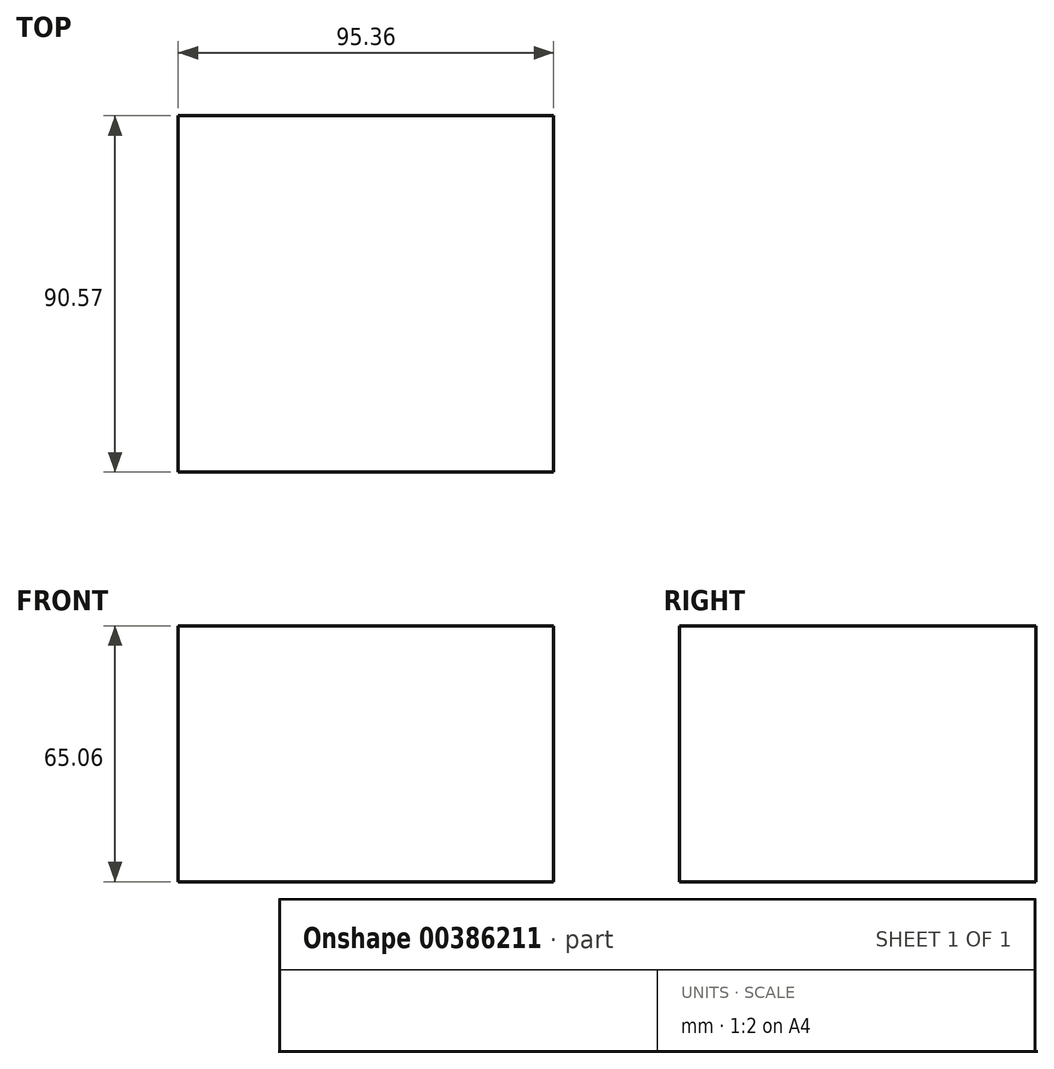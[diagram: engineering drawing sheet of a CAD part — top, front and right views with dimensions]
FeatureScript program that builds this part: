
annotation { "Feature Type Name" : "Feature", "Feature Type Description" : "" }
export const myFeature = defineFeature(function(context is Context, id is Id, definition is map)
    precondition{}
    {
        {
            var Q0;
            Q0=qCreatedBy(makeId("Top.planeOp"),FACE);
            var sketch = newSketch(context, id + "F0", { "sketchPlane" : qUnion([Q0])});
            skLineSegment(sketch, "E0.bottom", {"start": v(-31.38, 32.99) * mm, "end": v(63.98, 32.99) * mm});
            skLineSegment(sketch, "E0.top", {"start": v(-31.38, -57.58) * mm, "end": v(63.98, -57.58) * mm});
            skLineSegment(sketch, "E0.left", {"start": v(-31.38, 32.99) * mm, "end": v(-31.38, -57.58) * mm});
            skLineSegment(sketch, "E0.right", {"start": v(63.98, 32.99) * mm, "end": v(63.98, -57.58) * mm});
            skSolve(sketch);
        }
        {
            var Q0;
            Q0=makeQuery(id+"F0.imprint","IMPRINT",FACE,{"disambiguationData":[TD([[makeQuery(id+"F0.imprint","IMPRINT",EDGE,{"derivedFrom":sQuery(id+"F0.wireOp",EDGE,"E0.bottom")}),-1.0]])]});
            extrude(context, id + "F1", {"entities" : qUnion([Q0]), "depth" : 65.06 * mm});
        }
    });
